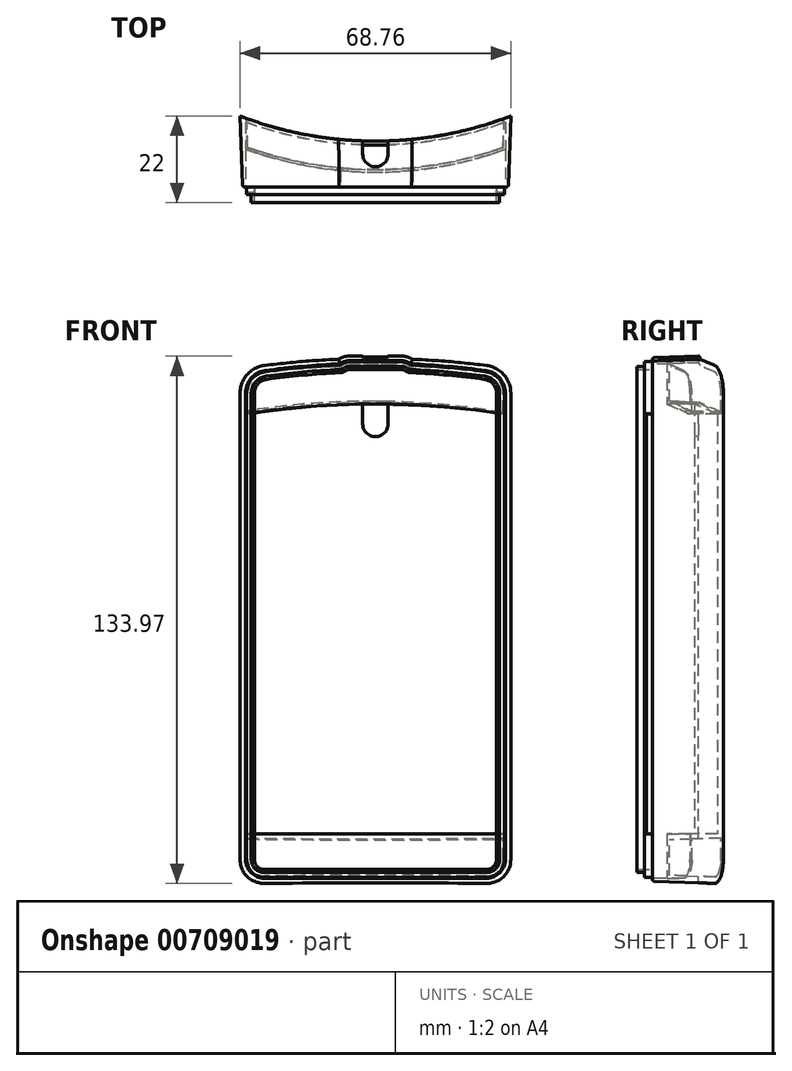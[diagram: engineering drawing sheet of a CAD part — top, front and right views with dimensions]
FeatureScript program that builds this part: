
annotation { "Feature Type Name" : "Feature", "Feature Type Description" : "" }
export const myFeature = defineFeature(function(context is Context, id is Id, definition is map)
    precondition{}
    {
        {
            var Q0;
            Q0=qCreatedBy(makeId("Front.planeOp"),FACE);
            var sketch = newSketch(context, id + "F0", { "sketchPlane" : qUnion([Q0])});
            skLineSegment(sketch, "E0.bottom", {"start": v(4.5, 0) * mm, "end": v(61, 0) * mm});
            skLineSegment(sketch, "E0.left", {"start": v(0, 4.5) * mm, "end": v(0, 123.05) * mm});
            skLineSegment(sketch, "E0.right", {"start": v(65.5, 4.5) * mm, "end": v(65.5, 123.05) * mm});
            skPoint(sketch, "E1.visualSharp", {"position": v(0, 0) * mm});
            skArc(sketch, "E1.filletArc", {"start": v(0, 4.5) * mm, "mid": v(1.32, 1.32) * mm, "end": v(4.5, 0) * mm});
            skPoint(sketch, "E2.visualSharp", {"position": v(65.5, 0) * mm});
            skArc(sketch, "E2.filletArc", {"start": v(61, 0) * mm, "mid": v(64.18, 1.32) * mm, "end": v(65.5, 4.5) * mm});
            skArc(sketch, "E3.filletArc", {"start": v(4.76, 128.5) * mm, "mid": v(1.36, 126.67) * mm, "end": v(0, 123.05) * mm});
            skPoint(sketch, "E4.visualSharp", {"position": v(65.5, 168.18) * mm});
            skArc(sketch, "E4.filletArc", {"start": v(65.5, 123.05) * mm, "mid": v(64.14, 126.67) * mm, "end": v(60.74, 128.5) * mm});
            skArc(sketch, "E5", {"start": v(60.74, 128.5) * mm, "mid": v(51.35, 129.57) * mm, "end": v(41.91, 130.2) * mm});
            skLineSegment(sketch, "E6", {"start": v(26, 131) * mm, "end": v(39.5, 131) * mm});
            skArc(sketch, "E7.trimOffspring", {"start": v(23.59, 130.2) * mm, "mid": v(14.15, 129.57) * mm, "end": v(4.76, 128.5) * mm});
            skLineSegment(sketch, "E8", {"start": v(32.75, 0) * mm, "end": v(32.75, 224.52) * mm, "construction": true});
            skArc(sketch, "E9", {"start": v(26, 131) * mm, "mid": v(25.02, 130.84) * mm, "end": v(24.13, 130.4) * mm});
            skPoint(sketch, "E10.visualSharp", {"position": v(23.91, 130.21) * mm});
            skArc(sketch, "E10.filletArc", {"start": v(23.59, 130.2) * mm, "mid": v(23.87, 130.26) * mm, "end": v(24.13, 130.4) * mm});
            skArc(sketch, "E11.MirrorCS", {"start": v(41.91, 130.2) * mm, "mid": v(41.63, 130.26) * mm, "end": v(41.37, 130.4) * mm});
            skArc(sketch, "E12.MirrorCS", {"start": v(39.5, 131) * mm, "mid": v(40.48, 130.84) * mm, "end": v(41.37, 130.4) * mm});
            skSolve(sketch);
        }
        {
            var Q0;
            Q0=qCreatedBy(makeId("Top.planeOp"),FACE);
            var sketch = newSketch(context, id + "F1", { "sketchPlane" : qUnion([Q0])});
            skArc(sketch, "E13", {"start": v(0, 0) * mm, "mid": v(32.75, -5.75) * mm, "end": v(65.5, 0) * mm});
            skLineSegment(sketch, "E14", {"start": v(0, 0) * mm, "end": v(65.5, 0) * mm});
            skLineSegment(sketch, "E15", {"start": v(0, 0) * mm, "end": v(94.5, 0) * mm, "construction": true});
            skLineSegment(sketch, "E16", {"start": v(94.5, 0) * mm, "end": v(32.75, 0) * mm, "construction": true});
            skLineSegment(sketch, "E17", {"start": v(32.75, 0) * mm, "end": v(32.75, -16.7) * mm, "construction": true});
            skSolve(sketch);
        }
        {
            var Q0;
            Q0 = qSketchRegion(id + "F0", true);
            extrude(context, id + "F2", {"entities" : qUnion([Q0]), "depth" : 12.5 * mm, "offsetDistance" : 25 * mm});
        }
        {
            var Q0;
            Q0 = qSketchRegion(id + "F1", true);
            extrude(context, id + "F3", {"entities" : qUnion([Q0]), "operationType" : NewBodyOperationType.REMOVE, "endBound" : BoundingType.THROUGH_ALL, "depth" : 25 * mm, "offsetDistance" : 25 * mm});
        }
        {
            var Q0;
            Q0=makeQuery(id+"F2.opExtrude","SWEPT_FACE",FACE,{"disambiguationData":[OSD([sQuery(id+"F0.wireOp",EDGE,"E0.bottom")])]});
            var sketch = newSketch(context, id + "F4", { "sketchPlane" : qUnion([Q0])});
            skLineSegment(sketch, "E18", {"start": v(0, 12.5) * mm, "end": v(0, 10.5) * mm});
            skLineSegment(sketch, "E19", {"start": v(0, 10.5) * mm, "end": v(1.1, 10.5) * mm});
            skLineSegment(sketch, "E20", {"start": v(1.1, 10.5) * mm, "end": v(1.1, 12.5) * mm});
            skLineSegment(sketch, "E21", {"start": v(1.1, 12.5) * mm, "end": v(0, 12.5) * mm});
            skSolve(sketch);
        }
        {
            var Q0;
            Q0=makeQuery(id+"F4.imprint","IMPRINT",FACE,{"disambiguationData":[TD([[makeQuery(id+"F4.imprint","IMPRINT",EDGE,{"derivedFrom":sQuery(id+"F4.wireOp",EDGE,"E18")}),1.0]])]});
            cPlane(context, id + "F5", {"entities" : qUnion([Q0]), "cplaneType" : CPlaneType.OFFSET, "offset" : 50 * mm, "oppositeDirection" : true, "width" : 150 * mm, "height" : 150 * mm});
        }
        {
            var Q0;
            Q0=makeQuery(id+"F2.opExtrude","CAP_FACE",FACE,{"disambiguationData":[OSD([sQuery(id+"F0.wireOp",EDGE,"E0.bottom"),sQuery(id+"F0.wireOp",EDGE,"E0.left"),sQuery(id+"F0.wireOp",EDGE,"E0.right"),sQuery(id+"F0.wireOp",EDGE,"E1.filletArc"),sQuery(id+"F0.wireOp",EDGE,"E2.filletArc"),sQuery(id+"F0.wireOp",EDGE,"E3.filletArc"),sQuery(id+"F0.wireOp",EDGE,"E4.filletArc"),sQuery(id+"F0.wireOp",EDGE,"E5"),sQuery(id+"F0.wireOp",EDGE,"E6"),sQuery(id+"F0.wireOp",EDGE,"4cuLOFSM-Cs9p-uLwk-Nxmp-eiNM5esqOte1"),sQuery(id+"F0.wireOp",EDGE,"qXNs2k06-4niP-ImqC-5Hru-JPzRlnRtqvzY"),sQuery(id+"F0.wireOp",EDGE,"592cab12-c6ad-4f12-8fa5-e9ea6a7a9ab5.filletArc"),sQuery(id+"F0.wireOp",EDGE,"E7.trimOffspring"),sQuery(id+"F0.wireOp",EDGE,"810a662d-7d86-4de4-b075-b749f1e53ed9.filletArc"),sQuery(id+"F0.wireOp",EDGE,"8d541c61-4af1-470d-ac14-312aa46fb37d.filletArc"),sQuery(id+"F0.wireOp",EDGE,"225b199f-dbc8-4900-9de2-33667acb90c7.filletArc")])],"isStart":false});
            shell(context, id + "F6", {"entities" : qUnion([Q0]), "thickness" : 2 * mm});
        }
        {
            var Q0;
            Q0=makeQuery(id+"F2.opExtrude","CAP_FACE",FACE,{"disambiguationData":[OSD([sQuery(id+"F0.wireOp",EDGE,"E0.bottom"),sQuery(id+"F0.wireOp",EDGE,"E0.left"),sQuery(id+"F0.wireOp",EDGE,"E0.right"),sQuery(id+"F0.wireOp",EDGE,"E1.filletArc"),sQuery(id+"F0.wireOp",EDGE,"E2.filletArc"),sQuery(id+"F0.wireOp",EDGE,"E3.filletArc"),sQuery(id+"F0.wireOp",EDGE,"E4.filletArc"),sQuery(id+"F0.wireOp",EDGE,"E5"),sQuery(id+"F0.wireOp",EDGE,"E6"),sQuery(id+"F0.wireOp",EDGE,"E7.trimOffspring"),sQuery(id+"F0.wireOp",EDGE,"E9"),sQuery(id+"F0.wireOp",EDGE,"E10.filletArc"),sQuery(id+"F0.wireOp",EDGE,"E11.MirrorCS"),sQuery(id+"F0.wireOp",EDGE,"E12.MirrorCS")])],"isStart":false});
            var sketch = newSketch(context, id + "F7", { "sketchPlane" : qUnion([Q0])});
            skLineSegment(sketch, "E22.0.0", {"start": v(39.5, 131) * mm, "end": v(26, 131) * mm});
            skArc(sketch, "E22.0.1", {"start": v(26, 131) * mm, "mid": v(25.02, 130.84) * mm, "end": v(24.13, 130.4) * mm});
            skArc(sketch, "E22.0.2", {"start": v(24.13, 130.4) * mm, "mid": v(23.87, 130.26) * mm, "end": v(23.59, 130.2) * mm});
            skArc(sketch, "E22.0.3", {"start": v(23.59, 130.2) * mm, "mid": v(14.15, 129.57) * mm, "end": v(4.76, 128.5) * mm});
            skArc(sketch, "E22.0.4", {"start": v(4.76, 128.5) * mm, "mid": v(1.36, 126.67) * mm, "end": v(0, 123.05) * mm});
            skLineSegment(sketch, "E22.0.5", {"start": v(0, 123.05) * mm, "end": v(0, 4.5) * mm});
            skArc(sketch, "E22.0.6", {"start": v(0, 4.5) * mm, "mid": v(1.32, 1.32) * mm, "end": v(4.5, 0) * mm});
            skLineSegment(sketch, "E22.0.7", {"start": v(4.5, 0) * mm, "end": v(61, 0) * mm});
            skArc(sketch, "E22.0.8", {"start": v(61, 0) * mm, "mid": v(64.18, 1.32) * mm, "end": v(65.5, 4.5) * mm});
            skLineSegment(sketch, "E22.0.9", {"start": v(65.5, 4.5) * mm, "end": v(65.5, 123.05) * mm});
            skArc(sketch, "E22.0.10", {"start": v(65.5, 123.05) * mm, "mid": v(64.14, 126.67) * mm, "end": v(60.74, 128.5) * mm});
            skArc(sketch, "E22.0.11", {"start": v(60.74, 128.5) * mm, "mid": v(51.35, 129.57) * mm, "end": v(41.91, 130.2) * mm});
            skArc(sketch, "E22.0.12", {"start": v(41.91, 130.2) * mm, "mid": v(41.63, 130.26) * mm, "end": v(41.37, 130.4) * mm});
            skArc(sketch, "E22.0.13", {"start": v(41.37, 130.4) * mm, "mid": v(40.48, 130.84) * mm, "end": v(39.5, 131) * mm});
            skArc(sketch, "E23.0", {"start": v(40.66, 129.42) * mm, "mid": v(40.1, 129.7) * mm, "end": v(39.5, 129.8) * mm});
            skArc(sketch, "E23.1", {"start": v(41.86, 129) * mm, "mid": v(41.23, 129.12) * mm, "end": v(40.66, 129.42) * mm});
            skArc(sketch, "E23.2", {"start": v(60.58, 127.31) * mm, "mid": v(51.24, 128.37) * mm, "end": v(41.86, 129) * mm});
            skArc(sketch, "E23.3", {"start": v(4.92, 127.31) * mm, "mid": v(2.26, 125.88) * mm, "end": v(1.2, 123.05) * mm});
            skArc(sketch, "E23.4", {"start": v(23.64, 129) * mm, "mid": v(14.26, 128.37) * mm, "end": v(4.92, 127.31) * mm});
            skArc(sketch, "E23.5", {"start": v(24.84, 129.42) * mm, "mid": v(24.27, 129.12) * mm, "end": v(23.64, 129) * mm});
            skArc(sketch, "E23.6", {"start": v(26, 129.8) * mm, "mid": v(25.4, 129.7) * mm, "end": v(24.84, 129.42) * mm});
            skLineSegment(sketch, "E23.7", {"start": v(1.2, 123.05) * mm, "end": v(1.2, 4.5) * mm});
            skArc(sketch, "E23.8", {"start": v(1.2, 4.5) * mm, "mid": v(2.17, 2.17) * mm, "end": v(4.5, 1.2) * mm});
            skLineSegment(sketch, "E23.9", {"start": v(4.5, 1.2) * mm, "end": v(61, 1.2) * mm});
            skLineSegment(sketch, "E23.10", {"start": v(39.5, 129.8) * mm, "end": v(26, 129.8) * mm});
            skArc(sketch, "E23.11", {"start": v(61, 1.2) * mm, "mid": v(63.33, 2.17) * mm, "end": v(64.3, 4.5) * mm});
            skLineSegment(sketch, "E23.12", {"start": v(64.3, 4.5) * mm, "end": v(64.3, 123.05) * mm});
            skArc(sketch, "E23.13", {"start": v(64.3, 123.05) * mm, "mid": v(63.24, 125.88) * mm, "end": v(60.58, 127.31) * mm});
            skSolve(sketch);
        }
        {
            var Q0;
            Q0 = qSketchRegion(id + "F7", true);
            extrude(context, id + "F8", {"entities" : qUnion([Q0]), "operationType" : NewBodyOperationType.REMOVE, "oppositeDirection" : true, "depth" : 2 * mm, "offsetDistance" : 25 * mm});
        }
        {
            var Q0;
            Q0=makeQuery(id+"F6.opShell","OFFSET_EDGE",EDGE,{"disambiguationData":[OSD([sQuery(id+"F0.wireOp",EDGE,"E7.trimOffspring")])]});
            var Q1;
            Q1=makeQuery(id+"F8.boolean.opBoolean","COPY",EDGE,{"derivedFrom":makeQuery(id+"F8.opExtrude","CAP_EDGE",EDGE,{"disambiguationData":[OSD([sQuery(id+"F7.wireOp",EDGE,"E23.4")])],"isStart":true})});
            fillet(context, id + "F9", {"entities" : qUnion([Q0, Q1]), "radius" : .2 * mm, "tangentPropagation" : true, "allowEdgeOverflow" : false});
        }
        {
            var Q0;
            Q0=qCreatedBy(makeId("Front.planeOp"),FACE);
            var sketch = newSketch(context, id + "F10", { "sketchPlane" : qUnion([Q0])});
            skCircle(sketch, "E24", {"center": v(52.88, 68) * mm, "radius": 5.12 * mm});
            skArc(sketch, "E25", {"start": v(16.47, 64.05) * mm, "mid": v(12.44, 73) * mm, "end": v(9.49, 63.64) * mm});
            skArc(sketch, "E26", {"start": v(10.62, 44.32) * mm, "mid": v(14.94, 30.41) * mm, "end": v(17.6, 44.73) * mm});
            skLineSegment(sketch, "E27", {"start": v(12.75, 67.75) * mm, "end": v(14.5, 37.9) * mm, "construction": true});
            skLineSegment(sketch, "E28", {"start": v(16.47, 64.05) * mm, "end": v(17.6, 44.73) * mm});
            skLineSegment(sketch, "E29.MirrorCS", {"start": v(9.49, 63.64) * mm, "end": v(10.62, 44.32) * mm});
            skSolve(sketch);
        }
        {
            var Q0;
            Q0 = qSketchRegion(id + "F10", true);
            extrude(context, id + "F11", {"entities" : qUnion([Q0]), "operationType" : NewBodyOperationType.REMOVE, "endBound" : BoundingType.THROUGH_ALL, "depth" : 25 * mm, "offsetDistance" : 25 * mm});
        }
        {
            var Q0;
            Q0=qCreatedBy(makeId("Front.planeOp"),FACE);
            var sketch = newSketch(context, id + "F12", { "sketchPlane" : qUnion([Q0])});
            skLineSegment(sketch, "E30", {"start": v(51.75, 114.46) * mm, "end": v(32.54, 67.75) * mm, "construction": true});
            skArc(sketch, "E31.0.startCap", {"start": v(49.2, 115.5) * mm, "mid": v(52.8, 117) * mm, "end": v(54.3, 113.41) * mm});
            skArc(sketch, "E31.0.endCap", {"start": v(35.09, 66.7) * mm, "mid": v(31.5, 65.2) * mm, "end": v(30, 68.8) * mm});
            skLineSegment(sketch, "E31.0.left", {"start": v(54.3, 113.41) * mm, "end": v(35.09, 66.7) * mm});
            skLineSegment(sketch, "E31.0.right", {"start": v(49.2, 115.5) * mm, "end": v(30, 68.8) * mm});
            skLineSegment(sketch, "E32.0", {"start": v(48.28, 115.89) * mm, "end": v(29.08, 69.18) * mm});
            skArc(sketch, "E32.1", {"start": v(48.28, 115.89) * mm, "mid": v(53.18, 117.93) * mm, "end": v(55.22, 113.03) * mm});
            skLineSegment(sketch, "E32.2", {"start": v(55.22, 113.03) * mm, "end": v(36.01, 66.32) * mm});
            skArc(sketch, "E32.3", {"start": v(36.01, 66.32) * mm, "mid": v(31.12, 64.28) * mm, "end": v(29.08, 69.18) * mm});
            skSolve(sketch);
        }
        {
            var Q0;
            {var subQ0=sQuery(id+"F1.wireOp",EDGE,"E14");var subQ1=sQuery(id+"F1.wireOp",EDGE,"E13");Q0=makeQuery(id+"F3.boolean.opBoolean","MERGE",EDGE,{"derivedFrom":[makeQuery(id+"F2.opExtrude","CAP_EDGE",EDGE,{"disambiguationData":[OSD([sQuery(id+"F0.wireOp",EDGE,"E0.left")])],"isStart":true}),makeQuery(id+"F3.opExtrude","SWEPT_EDGE",EDGE,{"disambiguationData":[OSD([subQ1,subQ0]),TDD([makeQuery(id+"F1.imprint","INTERSECT",VERTEX,{"disambiguationData":[OD(0.0)],"derivedFrom":[subQ1,subQ0]})])]})]});}
            fillet(context, id + "F13", {"entities" : qUnion([Q0]), "radius" : .5 * mm, "tangentPropagation" : true, "allowEdgeOverflow" : false});
        }
        {
            var Q0;
            Q0 = qSketchRegion(id + "F12", true);
            var Q1;
            Q1=makeQuery(id+"F3.boolean.opBoolean","COPY",FACE,{"derivedFrom":makeQuery(id+"F3.opExtrude","SWEPT_FACE",FACE,{"disambiguationData":[OSD([sQuery(id+"F1.wireOp",EDGE,"E13")])]})});
            var Q2;
            Q2=makeQuery(id+"F2.opExtrude","SWEPT_BODY",BODY,{"disambiguationData":[OSD([sQuery(id+"F0.wireOp",EDGE,"E0.bottom"),sQuery(id+"F0.wireOp",EDGE,"E0.left"),sQuery(id+"F0.wireOp",EDGE,"E0.right"),sQuery(id+"F0.wireOp",EDGE,"E1.filletArc"),sQuery(id+"F0.wireOp",EDGE,"E2.filletArc"),sQuery(id+"F0.wireOp",EDGE,"E3.filletArc"),sQuery(id+"F0.wireOp",EDGE,"E4.filletArc"),sQuery(id+"F0.wireOp",EDGE,"E5"),sQuery(id+"F0.wireOp",EDGE,"E6"),sQuery(id+"F0.wireOp",EDGE,"E7.trimOffspring"),sQuery(id+"F0.wireOp",EDGE,"E9"),sQuery(id+"F0.wireOp",EDGE,"E10.filletArc"),sQuery(id+"F0.wireOp",EDGE,"E11.MirrorCS"),sQuery(id+"F0.wireOp",EDGE,"E12.MirrorCS")])]});
            var Q3;
            Q3=makeQuery(id+"F3.boolean.opBoolean","COPY",FACE,{"derivedFrom":makeQuery(id+"F3.opExtrude","SWEPT_FACE",FACE,{"disambiguationData":[OSD([sQuery(id+"F1.wireOp",EDGE,"E13")])]})});
            extrude(context, id + "F14", {"entities" : qUnion([Q0]), "operationType" : NewBodyOperationType.ADD, "endBound" : BoundingType.UP_TO_SURFACE, "depth" : 25 * mm, "endBoundEntityFace" : qUnion([Q1]), "endBoundEntityBody" : qUnion([Q2]), "offsetDistance" : 1 * mm, "offsetOppositeDirection" : true, "hasSecondDirection" : true, "secondDirectionBound" : BoundingType.UP_TO_SURFACE, "secondDirectionOppositeDirection" : false, "secondDirectionDepth" : 1 * mm, "secondDirectionBoundEntityFace" : qUnion([Q3]), "hasSecondDirectionOffset" : true, "secondDirectionOffsetDistance" : .5 * mm});
        }
        {
            var Q0;
            Q0=makeQuery(id+"F14.opExtrude","CAP_EDGE",EDGE,{"disambiguationData":[OSD([sQuery(id+"F12.wireOp",EDGE,"E31.0.left")])],"isStart":true});
            var Q1;
            Q1=makeQuery(id+"F14.opExtrude","CAP_EDGE",EDGE,{"disambiguationData":[OSD([sQuery(id+"F12.wireOp",EDGE,"E32.2")])],"isStart":true});
            fillet(context, id + "F15", {"entities" : qUnion([Q0, Q1]), "radius" : .5 * mm, "tangentPropagation" : true, "allowEdgeOverflow" : false});
        }
        {
            var Q0;
            Q0=qCreatedBy(makeId("Front.planeOp"),FACE);
            var sketch = newSketch(context, id + "F16", { "sketchPlane" : qUnion([Q0])});
            skCircle(sketch, "E33", {"center": v(51.75, 114.46) * mm, "radius": 0.75 * mm});
            skLineSegment(sketch, "E34.0", {"start": v(51.75, 114.46) * mm, "end": v(32.54, 67.75) * mm, "construction": true});
            skSolve(sketch);
        }
        {
            var Q0;
            Q0=makeQuery(id+"F16.imprint","IMPRINT",FACE,{"disambiguationData":[TD([[makeQuery(id+"F16.imprint","IMPRINT",EDGE,{"derivedFrom":sQuery(id+"F16.wireOp",EDGE,"E33")}),1.0]])]});
            var Q1;
            Q1 = qConstructionFilter(qBodyType(qCreatedBy(id + "F16" ,EDGE), BodyType.WIRE), ConstructionObject.NO);
            extrude(context, id + "F17", {"entities" : qUnion([Q0]), "operationType" : NewBodyOperationType.REMOVE, "surfaceEntities" : qUnion([Q1]), "endBound" : BoundingType.THROUGH_ALL, "depth" : 25 * mm, "offsetDistance" : 25 * mm});
        }
        {
            var Q0;
            Q0=qCreatedBy(makeId("Top.planeOp"),FACE);
            var sketch = newSketch(context, id + "F18", { "sketchPlane" : qUnion([Q0])});
            skLineSegment(sketch, "E35.0", {"start": v(-0.5, -7.5) * mm, "end": v(-0.5, 1.21) * mm});
            skLineSegment(sketch, "E35.1", {"start": v(66, -7.57) * mm, "end": v(66, 1.14) * mm});
            skLineSegment(sketch, "E36", {"start": v(32.75, -4) * mm, "end": v(32.75, 0.99) * mm, "construction": true});
            skPoint(sketch, "E36.startSnap0", {"position": v(32.75, -4) * mm});
            skArc(sketch, "E37.0", {"start": v(66, 1.14) * mm, "mid": v(32.75, -4.75) * mm, "end": v(-0.5, 1.21) * mm});
            skSolve(sketch);
        }
        {
            var Q0;
            Q0=makeQuery(id+"F8.boolean.opBoolean","COPY",FACE,{"derivedFrom":makeQuery(id+"F8.opExtrude","CAP_FACE",FACE,{"disambiguationData":[OSD([sQuery(id+"F7.wireOp",EDGE,"E22.0.0"),sQuery(id+"F7.wireOp",EDGE,"E22.0.1"),sQuery(id+"F7.wireOp",EDGE,"E22.0.2"),sQuery(id+"F7.wireOp",EDGE,"E22.0.3"),sQuery(id+"F7.wireOp",EDGE,"E22.0.4"),sQuery(id+"F7.wireOp",EDGE,"E22.0.5"),sQuery(id+"F7.wireOp",EDGE,"E22.0.6"),sQuery(id+"F7.wireOp",EDGE,"E22.0.7"),sQuery(id+"F7.wireOp",EDGE,"E22.0.8"),sQuery(id+"F7.wireOp",EDGE,"E22.0.9"),sQuery(id+"F7.wireOp",EDGE,"E22.0.10"),sQuery(id+"F7.wireOp",EDGE,"E22.0.11"),sQuery(id+"F7.wireOp",EDGE,"E22.0.12"),sQuery(id+"F7.wireOp",EDGE,"E22.0.13"),sQuery(id+"F7.wireOp",EDGE,"E23.0"),sQuery(id+"F7.wireOp",EDGE,"E23.1"),sQuery(id+"F7.wireOp",EDGE,"E23.2"),sQuery(id+"F7.wireOp",EDGE,"E23.3"),sQuery(id+"F7.wireOp",EDGE,"E23.4"),sQuery(id+"F7.wireOp",EDGE,"E23.5"),sQuery(id+"F7.wireOp",EDGE,"E23.6"),sQuery(id+"F7.wireOp",EDGE,"E23.7"),sQuery(id+"F7.wireOp",EDGE,"E23.8"),sQuery(id+"F7.wireOp",EDGE,"E23.9"),sQuery(id+"F7.wireOp",EDGE,"E23.10"),sQuery(id+"F7.wireOp",EDGE,"E23.11"),sQuery(id+"F7.wireOp",EDGE,"E23.12"),sQuery(id+"F7.wireOp",EDGE,"E23.13")])],"isStart":false})});
            cPlane(context, id + "F19", {"entities" : qUnion([Q0]), "cplaneType" : CPlaneType.OFFSET, "offset" : 2 * mm, "oppositeDirection" : true, "width" : 150 * mm, "height" : 150 * mm});
        }
        {
            var Q0;
            Q0=qCreatedBy(id+"F19.planeOp",FACE);
            var sketch = newSketch(context, id + "F20", { "sketchPlane" : qUnion([Q0])});
            skLineSegment(sketch, "E38.0.0", {"start": v(39.5, 131) * mm, "end": v(26, 131) * mm});
            skArc(sketch, "E38.0.1", {"start": v(26, 131) * mm, "mid": v(25.02, 130.84) * mm, "end": v(24.13, 130.4) * mm});
            skArc(sketch, "E38.0.2", {"start": v(24.13, 130.4) * mm, "mid": v(23.87, 130.26) * mm, "end": v(23.59, 130.2) * mm});
            skArc(sketch, "E38.0.3", {"start": v(23.59, 130.2) * mm, "mid": v(14.15, 129.57) * mm, "end": v(4.76, 128.5) * mm});
            skArc(sketch, "E38.0.4", {"start": v(4.76, 128.5) * mm, "mid": v(1.36, 126.67) * mm, "end": v(0, 123.05) * mm});
            skLineSegment(sketch, "E38.0.5", {"start": v(0, 123.05) * mm, "end": v(0, 4.5) * mm});
            skArc(sketch, "E38.0.6", {"start": v(0, 4.5) * mm, "mid": v(1.32, 1.32) * mm, "end": v(4.5, 0) * mm});
            skLineSegment(sketch, "E38.0.7", {"start": v(4.5, 0) * mm, "end": v(61, 0) * mm});
            skArc(sketch, "E38.0.8", {"start": v(61, 0) * mm, "mid": v(64.18, 1.32) * mm, "end": v(65.5, 4.5) * mm});
            skLineSegment(sketch, "E38.0.9", {"start": v(65.5, 4.5) * mm, "end": v(65.5, 123.05) * mm});
            skArc(sketch, "E38.0.10", {"start": v(65.5, 123.05) * mm, "mid": v(64.14, 126.67) * mm, "end": v(60.74, 128.5) * mm});
            skArc(sketch, "E38.0.11", {"start": v(60.74, 128.5) * mm, "mid": v(51.35, 129.57) * mm, "end": v(41.91, 130.2) * mm});
            skArc(sketch, "E38.0.12", {"start": v(41.91, 130.2) * mm, "mid": v(41.63, 130.26) * mm, "end": v(41.37, 130.4) * mm});
            skArc(sketch, "E38.0.13", {"start": v(41.37, 130.4) * mm, "mid": v(40.48, 130.84) * mm, "end": v(39.5, 131) * mm});
            skLineSegment(sketch, "E39.0", {"start": v(4.5, -1) * mm, "end": v(61, -1) * mm});
            skArc(sketch, "E39.1", {"start": v(41.96, 131.2) * mm, "mid": v(40.8, 131.8) * mm, "end": v(39.5, 132) * mm});
            skArc(sketch, "E39.2", {"start": v(60.88, 129.5) * mm, "mid": v(51.44, 130.56) * mm, "end": v(41.96, 131.2) * mm});
            skArc(sketch, "E39.3", {"start": v(66.5, 123.05) * mm, "mid": v(64.9, 127.32) * mm, "end": v(60.88, 129.5) * mm});
            skLineSegment(sketch, "E39.4", {"start": v(66.5, 4.5) * mm, "end": v(66.5, 123.05) * mm});
            skLineSegment(sketch, "E39.5", {"start": v(39.5, 132) * mm, "end": v(26, 132) * mm});
            skArc(sketch, "E39.6", {"start": v(61, -1) * mm, "mid": v(64.89, 0.61) * mm, "end": v(66.5, 4.5) * mm});
            skArc(sketch, "E39.7", {"start": v(26, 132) * mm, "mid": v(24.7, 131.8) * mm, "end": v(23.54, 131.2) * mm});
            skArc(sketch, "E39.8", {"start": v(23.54, 131.2) * mm, "mid": v(14.06, 130.56) * mm, "end": v(4.62, 129.5) * mm});
            skArc(sketch, "E39.9", {"start": v(4.62, 129.5) * mm, "mid": v(0.6, 127.32) * mm, "end": v(-1, 123.05) * mm});
            skLineSegment(sketch, "E39.10", {"start": v(-1, 123.05) * mm, "end": v(-1, 4.5) * mm});
            skArc(sketch, "E39.11", {"start": v(-1, 4.5) * mm, "mid": v(0.61, 0.61) * mm, "end": v(4.5, -1) * mm});
            skArc(sketch, "E40.0", {"start": v(4.72, 128.75) * mm, "mid": v(1.17, 126.83) * mm, "end": v(-0.25, 123.05) * mm});
            skLineSegment(sketch, "E40.1", {"start": v(65.75, 4.5) * mm, "end": v(65.75, 123.05) * mm});
            skArc(sketch, "E40.2", {"start": v(61, -0.25) * mm, "mid": v(64.36, 1.14) * mm, "end": v(65.75, 4.5) * mm});
            skLineSegment(sketch, "E40.3", {"start": v(4.5, -0.25) * mm, "end": v(61, -0.25) * mm});
            skArc(sketch, "E40.4", {"start": v(-0.25, 4.5) * mm, "mid": v(1.14, 1.14) * mm, "end": v(4.5, -0.25) * mm});
            skArc(sketch, "E40.5", {"start": v(65.75, 123.05) * mm, "mid": v(64.33, 126.83) * mm, "end": v(60.78, 128.75) * mm});
            skLineSegment(sketch, "E40.6", {"start": v(-0.25, 123.05) * mm, "end": v(-0.25, 4.5) * mm});
            skArc(sketch, "E40.7", {"start": v(60.78, 128.75) * mm, "mid": v(51.25, 129.82) * mm, "end": v(41.68, 130.46) * mm});
            skArc(sketch, "E40.8", {"start": v(41.68, 130.46) * mm, "mid": v(40.66, 131.05) * mm, "end": v(39.5, 131.25) * mm});
            skLineSegment(sketch, "E40.9", {"start": v(39.5, 131.25) * mm, "end": v(26, 131.25) * mm});
            skArc(sketch, "E40.10", {"start": v(26, 131.25) * mm, "mid": v(24.84, 131.05) * mm, "end": v(23.82, 130.46) * mm});
            skArc(sketch, "E40.11", {"start": v(23.82, 130.46) * mm, "mid": v(14.25, 129.82) * mm, "end": v(4.72, 128.75) * mm});
            skSolve(sketch);
        }
        {
            var Q0;
            Q0=makeQuery(id+"F20.imprint","IMPRINT",FACE,{"disambiguationData":[TD([[makeQuery(id+"F20.imprint","IMPRINT",EDGE,{"derivedFrom":sQuery(id+"F20.wireOp",EDGE,"E38.0.0")}),-1.0]])]});
            var Q1;
            Q1=makeQuery(id+"F20.imprint","IMPRINT",FACE,{"disambiguationData":[TD([[makeQuery(id+"F20.imprint","IMPRINT",EDGE,{"derivedFrom":sQuery(id+"F20.wireOp",EDGE,"E38.0.0")}),1.0]])]});
            var Q2;
            Q2=makeQuery(id+"F20.imprint","IMPRINT",FACE,{"disambiguationData":[TD([[makeQuery(id+"F20.imprint","IMPRINT",EDGE,{"derivedFrom":sQuery(id+"F20.wireOp",EDGE,"E39.0")}),1.0]])]});
            extrude(context, id + "F21", {"entities" : qUnion([Q0, Q1, Q2]), "oppositeDirection" : true, "depth" : 18 * mm, "offsetDistance" : 25 * mm, "hasDraft" : true, "draftAngle" : 2 * degree});
        }
        {
            var Q0;
            Q0=qCreatedBy(makeId("Top.planeOp"),FACE);
            var sketch = newSketch(context, id + "F22", { "sketchPlane" : qUnion([Q0])});
            skLineSegment(sketch, "E41.0.0", {"start": v(61, -8.5) * mm, "end": v(4.5, -8.5) * mm, "construction": true});
            skLineSegment(sketch, "E41.0.1", {"start": v(4.5, 9.5) * mm, "end": v(4.5, -8.5) * mm, "construction": true});
            skLineSegment(sketch, "E41.0.2", {"start": v(4.5, 9.5) * mm, "end": v(61, 9.5) * mm, "construction": true});
            skLineSegment(sketch, "E41.0.3", {"start": v(61, 9.5) * mm, "end": v(61, -8.5) * mm, "construction": true});
            skLineSegment(sketch, "E41.1.0", {"start": v(66.5, -8.5) * mm, "end": v(61, -8.5) * mm, "construction": true});
            skLineSegment(sketch, "E41.1.1", {"start": v(61, 9.5) * mm, "end": v(61, -8.5) * mm, "construction": true});
            skLineSegment(sketch, "E41.1.2", {"start": v(61, 9.5) * mm, "end": v(67.13, 9.5) * mm, "construction": true});
            skLineSegment(sketch, "E41.1.3", {"start": v(67.13, 9.5) * mm, "end": v(66.5, -8.5) * mm, "construction": true});
            skLineSegment(sketch, "E41.2.0", {"start": v(4.5, -8.5) * mm, "end": v(-1, -8.5) * mm, "construction": true});
            skLineSegment(sketch, "E41.2.1", {"start": v(-1.63, 9.5) * mm, "end": v(-1, -8.5) * mm, "construction": true});
            skLineSegment(sketch, "E41.2.2", {"start": v(-1.63, 9.5) * mm, "end": v(4.5, 9.5) * mm, "construction": true});
            skLineSegment(sketch, "E41.2.3", {"start": v(4.5, 9.5) * mm, "end": v(4.5, -8.5) * mm, "construction": true});
            skArc(sketch, "E42", {"start": v(-1.63, 9.5) * mm, "mid": v(32.75, 3.14) * mm, "end": v(67.13, 9.5) * mm});
            skLineSegment(sketch, "E43", {"start": v(-1.63, 9.5) * mm, "end": v(67.13, 9.5) * mm});
            skSolve(sketch);
        }
        {
            var Q0;
            Q0=makeQuery(id+"F22.imprint","IMPRINT",FACE,{"disambiguationData":[TD([[makeQuery(id+"F22.imprint","IMPRINT",EDGE,{"derivedFrom":sQuery(id+"F22.wireOp",EDGE,"E42")}),1.0]])]});
            extrude(context, id + "F23", {"entities" : qUnion([Q0]), "operationType" : NewBodyOperationType.REMOVE, "endBound" : BoundingType.THROUGH_ALL, "oppositeDirection" : true, "depth" : 25 * mm, "offsetDistance" : 25 * mm, "hasSecondDirection" : true, "secondDirectionBound" : BoundingType.THROUGH_ALL, "secondDirectionOppositeDirection" : false, "secondDirectionDepth" : 25 * mm});
        }
        {
            var Q0;
            Q0=qCreatedBy(makeId("Top.planeOp"),FACE);
            cPlane(context, id + "F24", {"entities" : qUnion([Q0]), "cplaneType" : CPlaneType.OFFSET, "offset" : 6.5 * mm, "oppositeDirection" : true, "width" : 150 * mm, "height" : 150 * mm});
        }
        {
            var Q0;
            Q0=sQuery(id+"F18.wireOp",EDGE,"E37.0");
            extrude(context, id + "F25", {"bodyType" : ToolBodyType.SURFACE, "surfaceEntities" : qUnion([Q0]), "oppositeDirection" : true, "depth" : 5 * mm, "offsetDistance" : 25 * mm, "hasSecondDirection" : true, "secondDirectionOppositeDirection" : false, "secondDirectionDepth" : 150 * mm});
        }
        {
            var Q0;
            Q0=makeQuery(id+"F20.imprint","IMPRINT",FACE,{"disambiguationData":[TD([[makeQuery(id+"F20.imprint","IMPRINT",EDGE,{"derivedFrom":sQuery(id+"F20.wireOp",EDGE,"E38.0.0")}),-1.0]])]});
            var Q1;
            Q1=makeQuery(id+"F20.imprint","IMPRINT",FACE,{"disambiguationData":[TD([[makeQuery(id+"F20.imprint","IMPRINT",EDGE,{"derivedFrom":sQuery(id+"F20.wireOp",EDGE,"E38.0.0")}),1.0]])]});
            var Q2;
            Q2=makeQuery(id+"F25.opExtrude","SWEPT_FACE",FACE,{"disambiguationData":[OSD([sQuery(id+"F18.wireOp",EDGE,"E37.0")])]});
            extrude(context, id + "F26", {"entities" : qUnion([Q0, Q1]), "operationType" : NewBodyOperationType.REMOVE, "endBound" : BoundingType.UP_TO_SURFACE, "oppositeDirection" : true, "depth" : 25 * mm, "endBoundEntityFace" : qUnion([Q2]), "offsetDistance" : 25 * mm});
        }
        {
            var Q0;
            Q0=qCreatedBy(id+"F24.planeOp",FACE);
            var sketch = newSketch(context, id + "F27", { "sketchPlane" : qUnion([Q0])});
            skArc(sketch, "E44.0", {"start": v(-0.75, 1.9) * mm, "mid": v(32.75, -4.13) * mm, "end": v(66.25, 1.9) * mm});
            skLineSegment(sketch, "E45.0.0", {"start": v(39.5, -10.5) * mm, "end": v(39.5, -6.01) * mm, "construction": true});
            skArc(sketch, "E45.0.1", {"start": v(39.5, -6.01) * mm, "mid": v(32.75, -6.25) * mm, "end": v(26, -6.01) * mm, "construction": true});
            skLineSegment(sketch, "E45.0.2", {"start": v(26, -6.01) * mm, "end": v(26, -10.5) * mm, "construction": true});
            skLineSegment(sketch, "E45.0.3", {"start": v(26, -10.5) * mm, "end": v(39.5, -10.5) * mm, "construction": true});
            skLineSegment(sketch, "E46", {"start": v(32.75, -10.5) * mm, "end": v(32.75, 21.11) * mm, "construction": true});
            skPoint(sketch, "E46.endSnap0", {"position": v(32.75, -6.25) * mm});
            skSolve(sketch);
        }
        {
            var Q0;
            Q0=sQuery(id+"F27.wireOp",EDGE,"E44.0");
            extrude(context, id + "F28", {"bodyType" : ToolBodyType.SURFACE, "surfaceEntities" : qUnion([Q0]), "depth" : 147.2 * mm, "offsetDistance" : 25 * mm});
        }
        {
            var Q0;
            Q0=qCreatedBy(makeId("Front.planeOp"),FACE);
            cPlane(context, id + "F29", {"entities" : qUnion([Q0]), "cplaneType" : CPlaneType.OFFSET, "offset" : 10 * mm, "oppositeDirection" : true, "width" : 150 * mm, "height" : 150 * mm});
        }
        {
            var Q0;
            Q0=qCreatedBy(id+"F29.planeOp",FACE);
            var sketch = newSketch(context, id + "F30", { "sketchPlane" : qUnion([Q0])});
            skLineSegment(sketch, "E47.0", {"start": v(39.5, 131) * mm, "end": v(26, 131) * mm});
            skArc(sketch, "E47.1", {"start": v(26, 131) * mm, "mid": v(25.02, 130.84) * mm, "end": v(24.13, 130.4) * mm});
            skArc(sketch, "E47.2", {"start": v(24.13, 130.4) * mm, "mid": v(23.87, 130.26) * mm, "end": v(23.59, 130.2) * mm});
            skArc(sketch, "E47.3", {"start": v(23.59, 130.2) * mm, "mid": v(14.15, 129.57) * mm, "end": v(4.76, 128.5) * mm});
            skArc(sketch, "E47.4", {"start": v(4.76, 128.5) * mm, "mid": v(1.36, 126.67) * mm, "end": v(0, 123.05) * mm});
            skLineSegment(sketch, "E47.5", {"start": v(0, 123.05) * mm, "end": v(0, 118.18) * mm});
            skArc(sketch, "E47.6", {"start": v(0, 4.5) * mm, "mid": v(1.32, 1.32) * mm, "end": v(4.5, 0) * mm});
            skLineSegment(sketch, "E47.7", {"start": v(4.5, 0) * mm, "end": v(61, 0) * mm});
            skArc(sketch, "E47.8", {"start": v(61, 0) * mm, "mid": v(64.18, 1.32) * mm, "end": v(65.5, 4.5) * mm});
            skLineSegment(sketch, "E47.9", {"start": v(65.5, 4.5) * mm, "end": v(65.5, 10) * mm});
            skArc(sketch, "E47.10", {"start": v(65.5, 123.05) * mm, "mid": v(64.14, 126.67) * mm, "end": v(60.74, 128.5) * mm});
            skArc(sketch, "E47.11", {"start": v(60.74, 128.5) * mm, "mid": v(51.35, 129.57) * mm, "end": v(41.91, 130.2) * mm});
            skArc(sketch, "E47.12", {"start": v(41.91, 130.2) * mm, "mid": v(41.63, 130.26) * mm, "end": v(41.37, 130.4) * mm});
            skArc(sketch, "E47.13", {"start": v(41.37, 130.4) * mm, "mid": v(40.48, 130.84) * mm, "end": v(39.5, 131) * mm});
            skLineSegment(sketch, "E48", {"start": v(0, 10) * mm, "end": v(65.5, 10) * mm});
            skArc(sketch, "E49", {"start": v(65.5, 117.73) * mm, "mid": v(32.77, 120.45) * mm, "end": v(0, 118.18) * mm});
            skLineSegment(sketch, "E50.trimOffspring", {"start": v(0, 10) * mm, "end": v(0, 4.5) * mm});
            skLineSegment(sketch, "E51.trimOffspring", {"start": v(65.5, 117.73) * mm, "end": v(65.5, 123.05) * mm});
            skSolve(sketch);
        }
        {
            var Q0;
            Q0 = qSketchRegion(id + "F30", true);
            var Q1;
            Q1=makeQuery(id+"F28.opExtrude","SWEPT_FACE",FACE,{"disambiguationData":[OSD([sQuery(id+"F27.wireOp",EDGE,"E44.0")])]});
            extrude(context, id + "F31", {"entities" : qUnion([Q0]), "operationType" : NewBodyOperationType.REMOVE, "endBound" : BoundingType.UP_TO_SURFACE, "depth" : 25 * mm, "endBoundEntityFace" : qUnion([Q1]), "offsetDistance" : 25 * mm, "hasDraft" : true, "draftAngle" : 2 * degree, "draftPullDirection" : true});
        }
        {
            var Q0;
            Q0=qCreatedBy(makeId("Front.planeOp"),FACE);
            cPlane(context, id + "F32", {"entities" : qUnion([Q0]), "cplaneType" : CPlaneType.OFFSET, "offset" : 10 * mm, "width" : 150 * mm, "height" : 150 * mm});
        }
        {
            var Q0;
            Q0=qCreatedBy(id+"F32.planeOp",FACE);
            var sketch = newSketch(context, id + "F33", { "sketchPlane" : qUnion([Q0])});
            skLineSegment(sketch, "E52", {"start": v(-0.25, 117.69) * mm, "end": v(-0.25, 11) * mm});
            skLineSegment(sketch, "E53", {"start": v(65.75, 117.69) * mm, "end": v(65.75, 11) * mm});
            skLineSegment(sketch, "E54", {"start": v(-0.25, 11) * mm, "end": v(65.75, 11) * mm});
            skArc(sketch, "E55", {"start": v(65.75, 117.69) * mm, "mid": v(32.75, 120.23) * mm, "end": v(-0.25, 117.69) * mm});
            skLineSegment(sketch, "E56.0", {"start": v(4.5, -0.25) * mm, "end": v(61, -0.25) * mm, "construction": true});
            skLineSegment(sketch, "E57", {"start": v(32.75, -0.25) * mm, "end": v(32.75, 50.5) * mm, "construction": true});
            skSolve(sketch);
        }
        {
            var Q0;
            Q0=sQuery(id+"F22.wireOp",EDGE,"E42");
            extrude(context, id + "F34", {"bodyType" : ToolBodyType.SURFACE, "surfaceEntities" : qUnion([Q0]), "oppositeDirection" : true, "depth" : 10 * mm, "offsetDistance" : 25 * mm, "hasSecondDirection" : true, "secondDirectionOppositeDirection" : false, "secondDirectionDepth" : 141.6 * mm});
        }
        {
            var Q0;
            Q0=makeQuery(id+"F34.opExtrude","SWEPT_BODY",BODY,{"disambiguationData":[OSD([sQuery(id+"F22.wireOp",EDGE,"E42")])]});
            transform(context, id + "F35", {"entities" : qUnion([Q0]), "transformType" : TransformType.TRANSLATION_3D, "dx" : 0 * mm, "dy" : -1 * mm, "dz" : 0 * mm, "makeCopy" : false});
        }
        {
            var Q0;
            Q0 = qSketchRegion(id + "F33", true);
            var Q1;
            Q1=makeQuery(id+"F34.opExtrude","SWEPT_FACE",FACE,{"disambiguationData":[OSD([sQuery(id+"F22.wireOp",EDGE,"E42")])]});
            extrude(context, id + "F36", {"entities" : qUnion([Q0]), "operationType" : NewBodyOperationType.REMOVE, "endBound" : BoundingType.UP_TO_SURFACE, "oppositeDirection" : true, "depth" : 25 * mm, "endBoundEntityFace" : qUnion([Q1]), "offsetDistance" : 25 * mm});
        }
        {
            var Q0;
            Q0=qCreatedBy(makeId("Top.planeOp"),FACE);
            cPlane(context, id + "F37", {"entities" : qUnion([Q0]), "cplaneType" : CPlaneType.OFFSET, "offset" : 140.2 * mm, "width" : 150 * mm, "height" : 150 * mm});
        }
        {
            var Q0;
            Q0=qCreatedBy(id+"F37.planeOp",FACE);
            var sketch = newSketch(context, id + "F38", { "sketchPlane" : qUnion([Q0])});
            skLineSegment(sketch, "E58.0.0", {"start": v(26, 3.38) * mm, "end": v(26, -6.5) * mm, "construction": true});
            skLineSegment(sketch, "E58.0.1", {"start": v(26, -6.5) * mm, "end": v(39.5, -6.5) * mm, "construction": true});
            skLineSegment(sketch, "E58.0.2", {"start": v(39.5, 3.38) * mm, "end": v(39.5, -6.5) * mm, "construction": true});
            skArc(sketch, "E58.0.3", {"start": v(36, 3.2) * mm, "mid": v(32.75, 3.14) * mm, "end": v(29.5, 3.2) * mm});
            skLineSegment(sketch, "E59", {"start": v(32.75, -6.5) * mm, "end": v(32.75, 3.14) * mm, "construction": true});
            skLineSegment(sketch, "E60", {"start": v(29.5, 3.2) * mm, "end": v(29.5, -0.1) * mm});
            skLineSegment(sketch, "E61.MirrorCS", {"start": v(36, 3.2) * mm, "end": v(36, -0.1) * mm});
            skArc(sketch, "E62", {"start": v(29.5, -0.1) * mm, "mid": v(32.75, -3.36) * mm, "end": v(36, -0.1) * mm});
            skSolve(sketch);
        }
        {
            var Q0;
            Q0 = qSketchRegion(id + "F38", true);
            var Q1;
            Q1=makeQuery(id+"F36.boolean.opBoolean","COPY",FACE,{"derivedFrom":makeQuery(id+"F36.opExtrude","SWEPT_FACE",FACE,{"disambiguationData":[OSD([sQuery(id+"F33.wireOp",EDGE,"E55")])]})});
            extrude(context, id + "F39", {"entities" : qUnion([Q0]), "operationType" : NewBodyOperationType.REMOVE, "endBound" : BoundingType.UP_TO_SURFACE, "oppositeDirection" : true, "depth" : 25 * mm, "endBoundEntityFace" : qUnion([Q1]), "hasOffset" : true, "offsetDistance" : 5 * mm, "offsetOppositeDirection" : true});
        }
        {
            var Q0;
            Q0=makeQuery(id+"F21.opExtrude","CAP_EDGE",EDGE,{"disambiguationData":[OSD([sQuery(id+"F20.wireOp",EDGE,"E39.2")])],"isStart":true});
            var Q1;
            Q1=makeQuery(id+"F21.opExtrude","CAP_EDGE",EDGE,{"disambiguationData":[OSD([sQuery(id+"F20.wireOp",EDGE,"E39.1")])],"isStart":true});
            fillet(context, id + "F40", {"entities" : qUnion([Q0, Q1]), "radius" : .5 * mm, "tangentPropagation" : true, "allowEdgeOverflow" : false});
        }
        {
            var Q0;
            Q0=qCreatedBy(makeId("Front.planeOp"),FACE);
            var sketch = newSketch(context, id + "F41", { "sketchPlane" : qUnion([Q0])});
            skArc(sketch, "E63.0", {"start": v(36, 115.2) * mm, "mid": v(32.75, 115.23) * mm, "end": v(29.5, 115.2) * mm});
            skArc(sketch, "E64", {"start": v(29.5, 115.2) * mm, "mid": v(32.75, 111.98) * mm, "end": v(36, 115.2) * mm});
            skSolve(sketch);
        }
        {
            var Q0;
            Q0=makeQuery(id+"F41.imprint","IMPRINT",FACE,{"disambiguationData":[TD([[makeQuery(id+"F41.imprint","IMPRINT",EDGE,{"derivedFrom":sQuery(id+"F41.wireOp",EDGE,"E63.0")}),1.0]])]});
            extrude(context, id + "F42", {"entities" : qUnion([Q0]), "operationType" : NewBodyOperationType.REMOVE, "endBound" : BoundingType.THROUGH_ALL, "oppositeDirection" : true, "depth" : 25 * mm, "offsetDistance" : 25 * mm});
        }
    });
